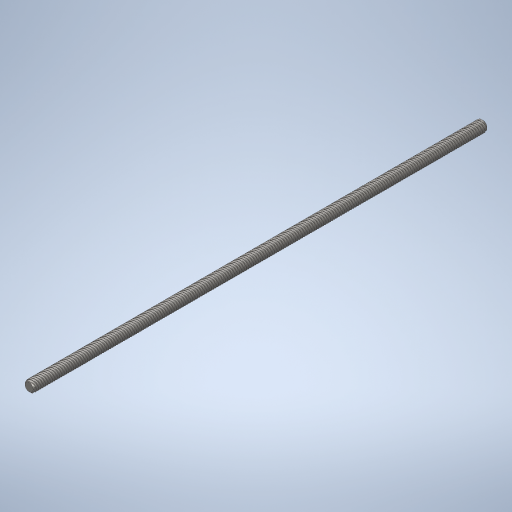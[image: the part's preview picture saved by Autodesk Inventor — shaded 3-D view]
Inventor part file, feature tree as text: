
AUTODESK INVENTOR PART (.ipt)
format: ipt  version: 2024.2 (Build 282272000, 272)  size: 1,574,912 bytes
history: native  units: mm
features: helix x2, extrude x1, sketch x1, chamfer x1
ambient origin geometry x8: Origin, YZ Plane, XZ Plane, XY Plane, X Axis, Y Axis, Z Axis, Center Point
bodies: Solid1 (feature_tree)
feature tree (5):
  extrude  "Extrusion1"  Depth=10.0mm TaperAngle=0.0deg
  sketch  "Sketch2"  dims[d0=8.0mm d1=340.0mm d2=0.0mm d3=1.4mm d4=4.0mm d13=1.0mm d14=2.0mm d15=45.0deg d16=1.4mm d17=1.4mm d18=1.4mm d19=7.0mm d20=10.0mm d21=2000.0mm d22=0.0mm d23=90.0deg d24=90.0deg d25=0.0mm d26=0.0mm d35=7.0mm d36=10.0mm d37=2000.0mm d38=0.0mm d39=90.0deg d40=90.0deg d41=0.0mm d42=0.0mm]
  chamfer  "Chamfer1"  Distance=1.4mm
  helix  "Coil2"  [1 undecoded]
  helix  "Coil4"  [1 undecoded]
note: 2 required parameter values undecoded (feature->parameter linkage not recoverable at this tier; creation-order binding heuristic only, values carry confidence <= 0.55)
